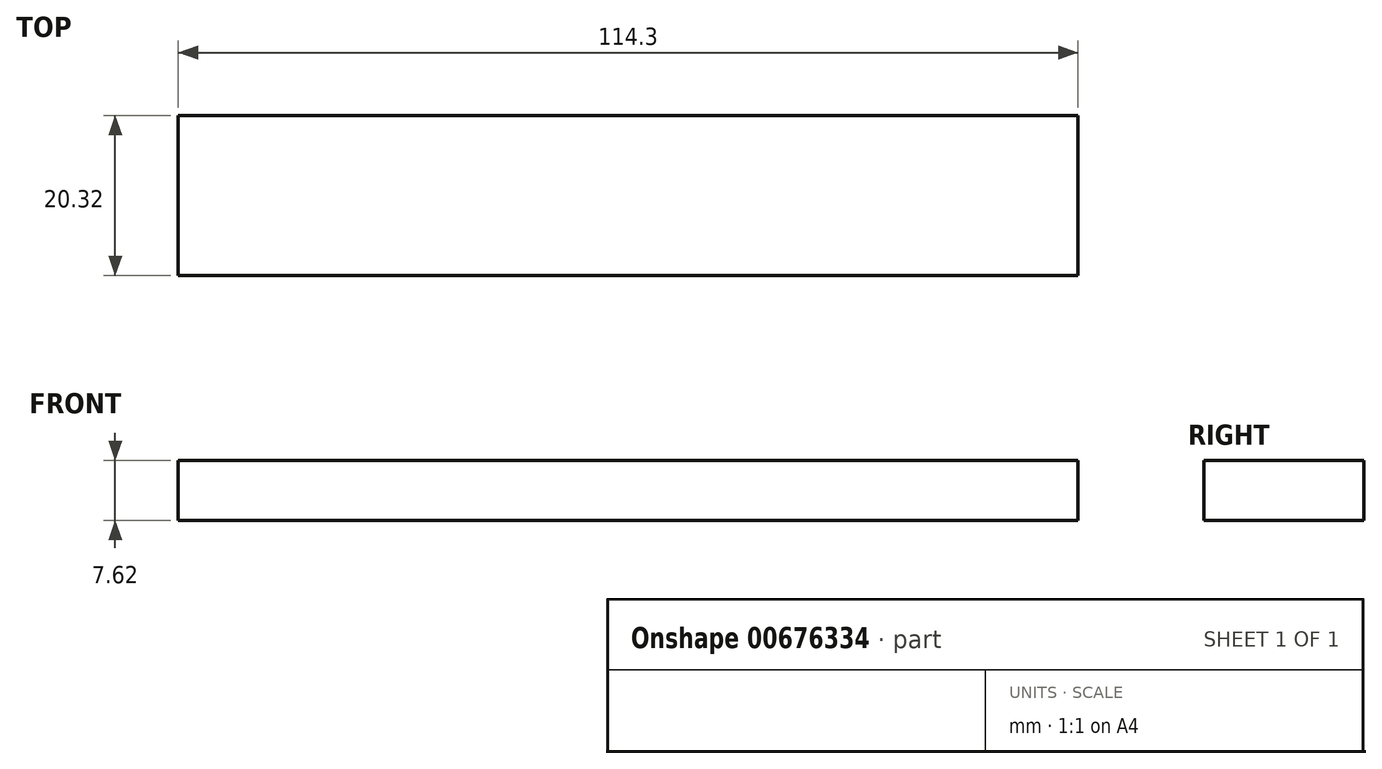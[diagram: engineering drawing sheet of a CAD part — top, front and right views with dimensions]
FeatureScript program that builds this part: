
annotation { "Feature Type Name" : "Feature", "Feature Type Description" : "" }
export const myFeature = defineFeature(function(context is Context, id is Id, definition is map)
    precondition{}
    {
        {
            var Q0;
            Q0=qCreatedBy(makeId("Front.planeOp"),FACE);
            var sketch = newSketch(context, id + "F0", { "sketchPlane" : qUnion([Q0])});
            skLineSegment(sketch, "E0", {"start": v(0, 0) * mm, "end": v(-114.3, 0) * mm});
            skLineSegment(sketch, "E1", {"start": v(-114.3, 7.62) * mm, "end": v(0, 7.62) * mm});
            skLineSegment(sketch, "E2", {"start": v(0, 7.62) * mm, "end": v(0, 0) * mm});
            skLineSegment(sketch, "E3", {"start": v(-114.3, 7.62) * mm, "end": v(-114.3, 0) * mm});
            skSolve(sketch);
        }
        {
            var Q0;
            Q0 = qSketchRegion(id + "F0", true);
            extrude(context, id + "F1", {"entities" : qUnion([Q0]), "depth" : 20.32 * mm, "offsetDistance" : 25.4 * mm});
        }
    });
